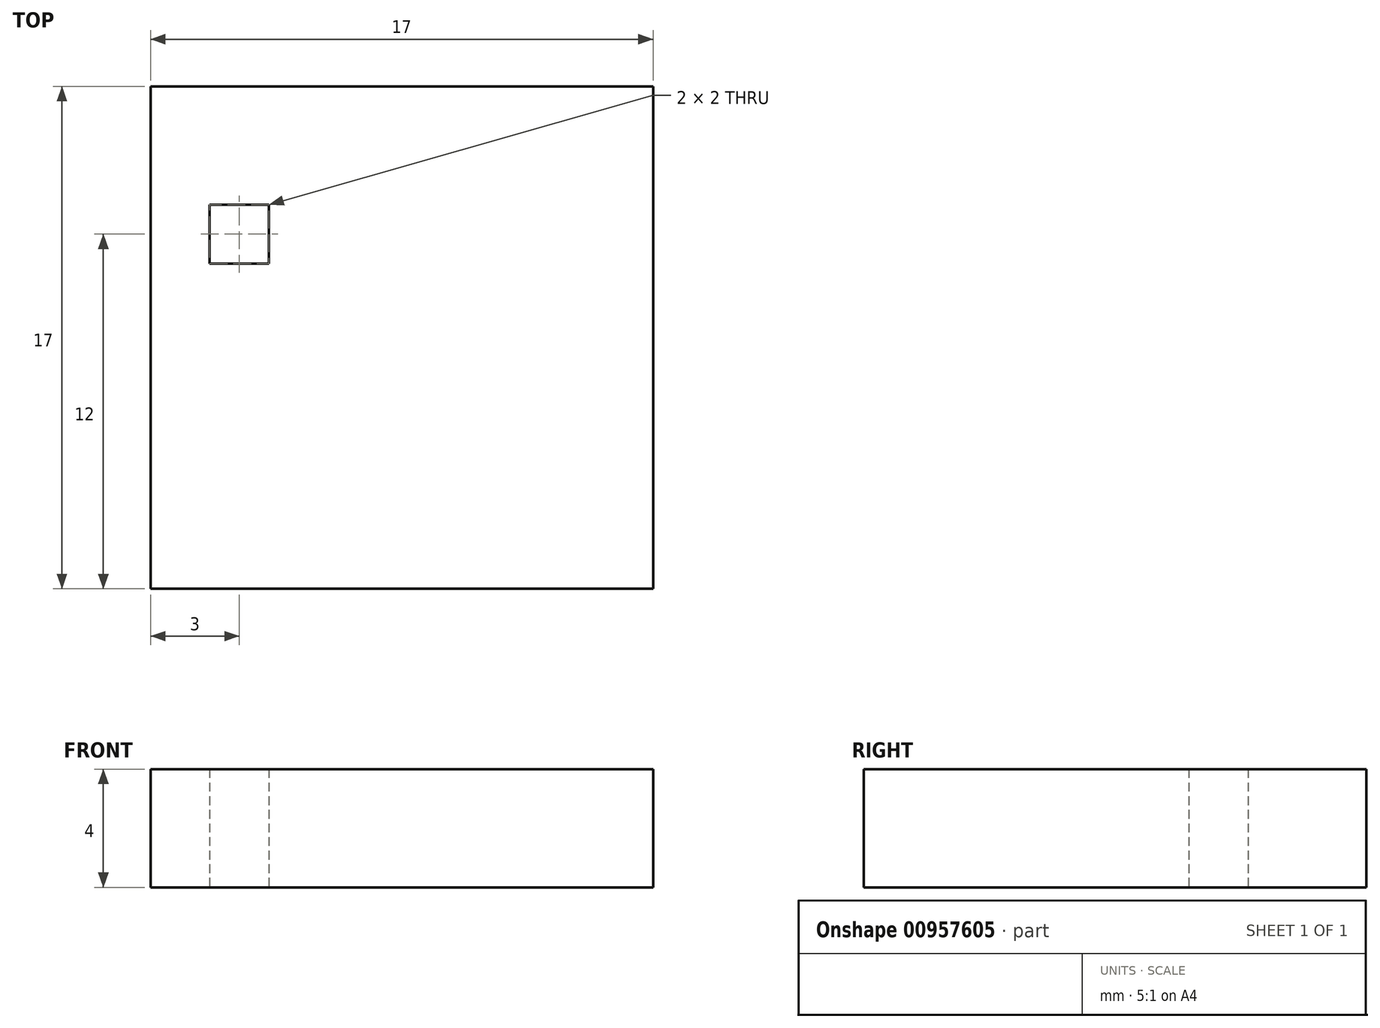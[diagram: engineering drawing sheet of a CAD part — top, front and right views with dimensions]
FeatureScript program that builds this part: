
annotation { "Feature Type Name" : "Feature", "Feature Type Description" : "" }
export const myFeature = defineFeature(function(context is Context, id is Id, definition is map)
    precondition{}
    {
        {
            var Q0;
            Q0=qCreatedBy(makeId("Top.planeOp"),FACE);
            var sketch = newSketch(context, id + "F0", { "sketchPlane" : qUnion([Q0])});
            skLineSegment(sketch, "E0.bottom", {"start": v(-8.5, 8.5) * mm, "end": v(8.5, 8.5) * mm});
            skLineSegment(sketch, "E0.top", {"start": v(-8.5, -8.5) * mm, "end": v(8.5, -8.5) * mm});
            skLineSegment(sketch, "E0.left", {"start": v(-8.5, 8.5) * mm, "end": v(-8.5, -8.5) * mm});
            skLineSegment(sketch, "E0.right", {"start": v(8.5, 8.5) * mm, "end": v(8.5, -8.5) * mm});
            skPoint(sketch, "E0.middle", {"position": v(0, 0) * mm});
            skLineSegment(sketch, "E1.bottom", {"start": v(-4.5, 4.5) * mm, "end": v(-6.5, 4.5) * mm});
            skLineSegment(sketch, "E1.top", {"start": v(-4.5, 2.5) * mm, "end": v(-6.5, 2.5) * mm});
            skLineSegment(sketch, "E1.left", {"start": v(-4.5, 4.5) * mm, "end": v(-4.5, 2.5) * mm});
            skLineSegment(sketch, "E1.right", {"start": v(-6.5, 4.5) * mm, "end": v(-6.5, 2.5) * mm});
            skSolve(sketch);
        }
        {
            var Q0;
            Q0=makeQuery(id+"F0.imprint","IMPRINT",FACE,{"disambiguationData":[TD([[makeQuery(id+"F0.imprint","IMPRINT",EDGE,{"derivedFrom":sQuery(id+"F0.wireOp",EDGE,"E0.bottom")}),-1.0]])]});
            extrude(context, id + "F1", {"entities" : qUnion([Q0]), "depth" : 4 * mm, "offsetDistance" : 25 * mm});
        }
    });
